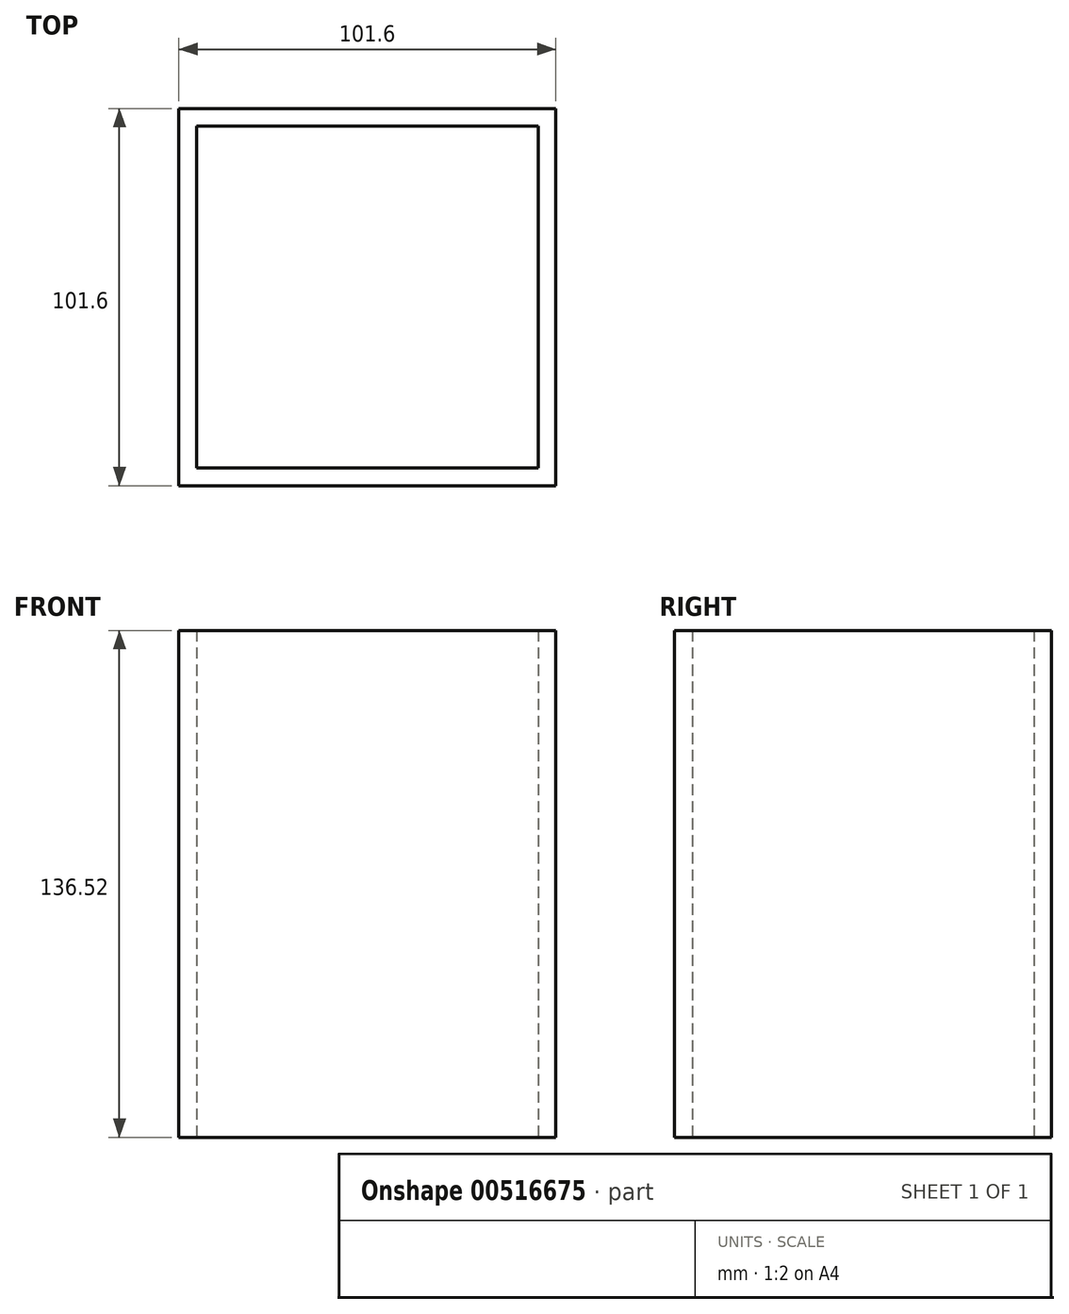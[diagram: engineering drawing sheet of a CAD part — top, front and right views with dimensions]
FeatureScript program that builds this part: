
annotation { "Feature Type Name" : "Feature", "Feature Type Description" : "" }
export const myFeature = defineFeature(function(context is Context, id is Id, definition is map)
    precondition{}
    {
        {
            var Q0;
            Q0=qCreatedBy(makeId("Top.planeOp"),FACE);
            var sketch = newSketch(context, id + "F0", { "sketchPlane" : qUnion([Q0])});
            skLineSegment(sketch, "E0.bottom", {"start": v(50.8, 50.8) * mm, "end": v(-50.8, 50.8) * mm});
            skLineSegment(sketch, "E0.top", {"start": v(50.8, -50.8) * mm, "end": v(-50.8, -50.8) * mm});
            skLineSegment(sketch, "E0.left", {"start": v(50.8, 50.8) * mm, "end": v(50.8, -50.8) * mm});
            skLineSegment(sketch, "E0.right", {"start": v(-50.8, 50.8) * mm, "end": v(-50.8, -50.8) * mm});
            skPoint(sketch, "E0.middle", {"position": v(0, 0) * mm});
            skLineSegment(sketch, "E1.bottom", {"start": v(46.04, 46.04) * mm, "end": v(-46.04, 46.04) * mm});
            skLineSegment(sketch, "E1.top", {"start": v(46.04, -46.04) * mm, "end": v(-46.04, -46.04) * mm});
            skLineSegment(sketch, "E1.left", {"start": v(46.04, 46.04) * mm, "end": v(46.04, -46.04) * mm});
            skLineSegment(sketch, "E1.right", {"start": v(-46.04, 46.04) * mm, "end": v(-46.04, -46.04) * mm});
            skSolve(sketch);
        }
        {
            var Q0;
            Q0 = qSketchRegion(id + "F0", true);
            extrude(context, id + "F1", {"entities" : qUnion([Q0]), "endBound" : BoundingType.SYMMETRIC, "depth" : 136.53 * mm, "offsetDistance" : 25.4 * mm});
        }
    });
